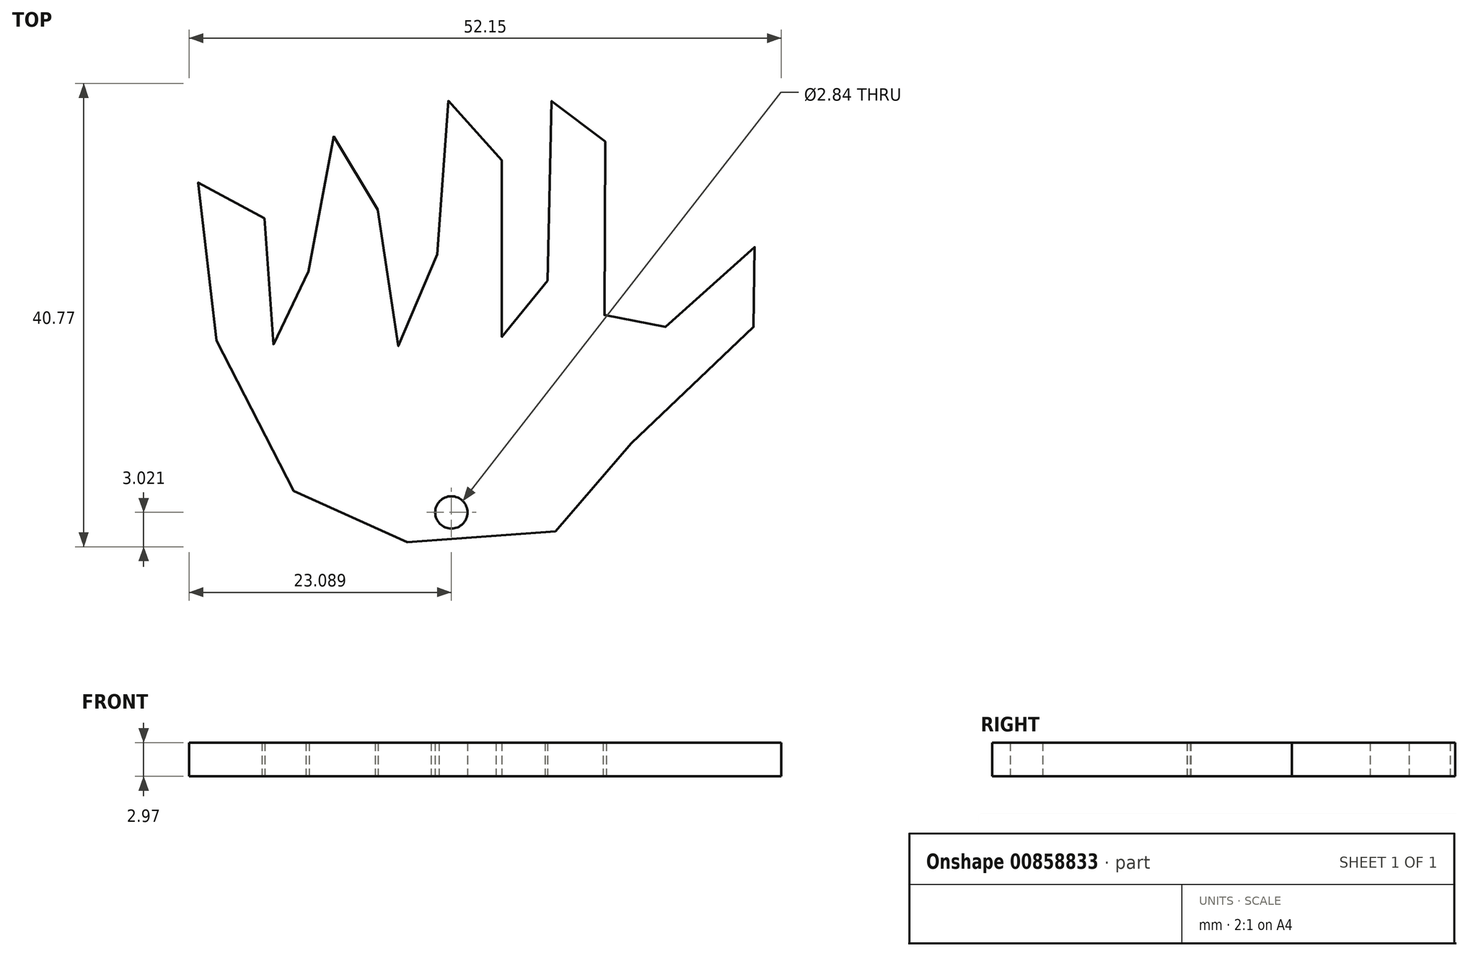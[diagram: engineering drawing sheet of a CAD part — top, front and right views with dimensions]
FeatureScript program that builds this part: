
annotation { "Feature Type Name" : "Feature", "Feature Type Description" : "" }
export const myFeature = defineFeature(function(context is Context, id is Id, definition is map)
    precondition{}
    {
        {
            var Q0;
            Q0=qCreatedBy(makeId("Top.planeOp"),FACE);
            var sketch = newSketch(context, id + "F0", { "sketchPlane" : qUnion([Q0])});
            skFitSpline(sketch, "E0", {"points": [v(0, 0) * mm, v(7.3, 8.48) * mm, v(19.88, 22.13) * mm, v(16.51, 24.96) * mm, v(7.83, 16.28) * mm, v(4.64, 17.52) * mm, v(3.58, 37.72) * mm, v(0, 38.6) * mm, v(-1.56, 16.99) * mm, v(-4.58, 16.8) * mm, v(-5.64, 38.08) * mm, v(-10.25, 36.66) * mm, v(-10.96, 17.52) * mm, v(-15.03, 17.34) * mm, v(-16.45, 34.7) * mm, v(-21.24, 32.58) * mm, v(-22.3, 16.99) * mm, v(-25.31, 16.99) * mm, v(-26.38, 30.46) * mm, v(-31.51, 30.63) * mm, v(-26.02, 8.13) * mm, v(-17.34, 0) * mm, v(0, 0) * mm]});
            skCircle(sketch, "E1", {"center": v(-9.17, 1.67) * mm, "radius": 1.42 * mm});
            skSolve(sketch);
        }
        {
            var Q0;
            Q0 = qSketchRegion(id + "F0", true);
            extrude(context, id + "F1", {"entities" : qUnion([Q0]), "depth" : 2.97 * mm, "offsetDistance" : 25.4 * mm});
        }
    });
